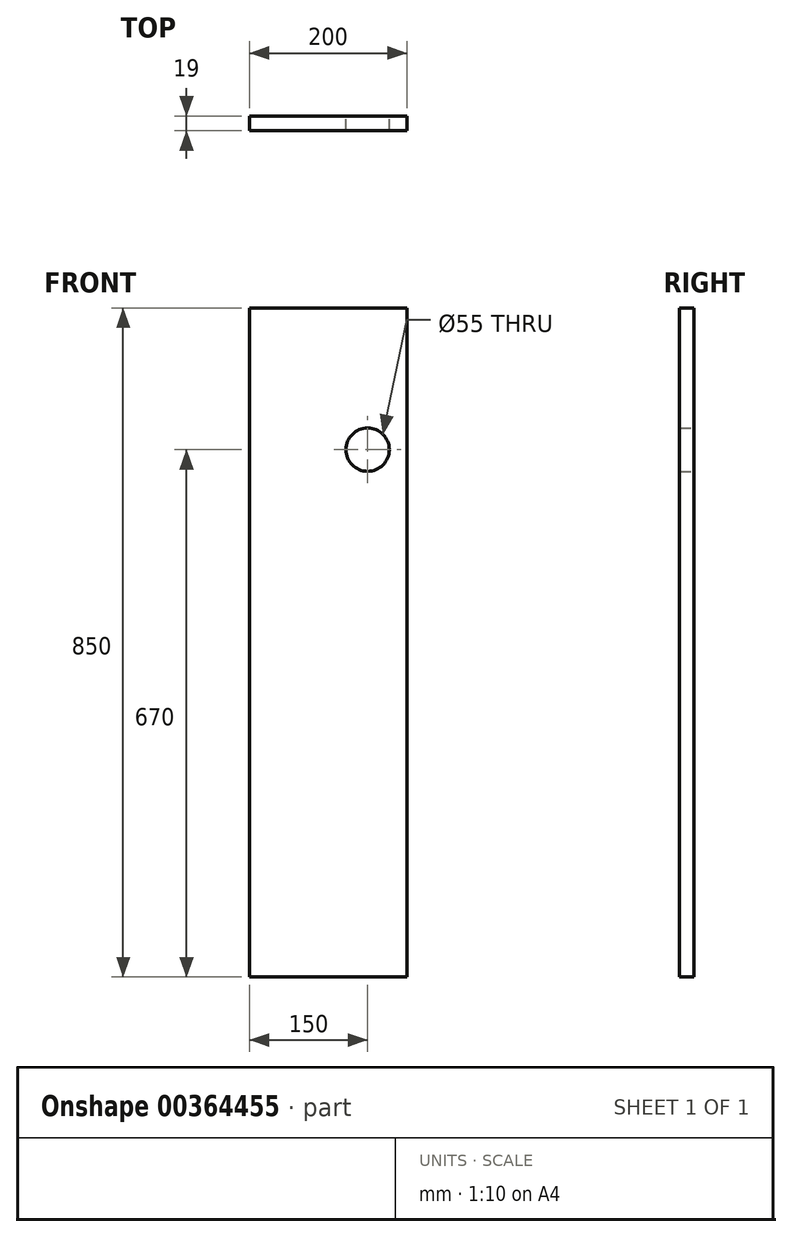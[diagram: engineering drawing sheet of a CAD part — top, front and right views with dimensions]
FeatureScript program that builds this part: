
annotation { "Feature Type Name" : "Feature", "Feature Type Description" : "" }
export const myFeature = defineFeature(function(context is Context, id is Id, definition is map)
    precondition{}
    {
        {
            var Q0;
            Q0=qCreatedBy(makeId("Front.planeOp"),FACE);
            var sketch = newSketch(context, id + "F0", { "sketchPlane" : qUnion([Q0])});
            skLineSegment(sketch, "E0.bottom", {"start": v(200, 850) * mm, "end": v(0, 850) * mm});
            skLineSegment(sketch, "E0.top", {"start": v(200, 0) * mm, "end": v(0, 0) * mm});
            skLineSegment(sketch, "E0.left", {"start": v(200, 850) * mm, "end": v(200, 0) * mm});
            skLineSegment(sketch, "E0.right", {"start": v(0, 850) * mm, "end": v(0, 0) * mm});
            skCircle(sketch, "E1", {"center": v(150, 670) * mm, "radius": 27.5 * mm});
            skSolve(sketch);
        }
        {
            var Q0;
            Q0=makeQuery(id+"F0.imprint","IMPRINT",FACE,{"disambiguationData":[TD([[makeQuery(id+"F0.imprint","IMPRINT",EDGE,{"derivedFrom":sQuery(id+"F0.wireOp",EDGE,"E0.bottom")}),1.0]])]});
            extrude(context, id + "F1", {"entities" : qUnion([Q0]), "depth" : 19 * mm});
        }
    });
